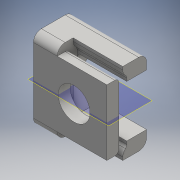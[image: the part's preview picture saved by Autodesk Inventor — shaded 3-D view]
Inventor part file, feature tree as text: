
AUTODESK INVENTOR PART (.ipt)
format: ipt  version: 2016 (Build 200138000, 138)  size: 255,488 bytes
history: native  units: mm
features: extrude x12, sketch x12, projected_geometry x5, fillet x3, plane x1, mirror x1
ambient origin geometry x8: Origin, YZ Plane, XZ Plane, XY Plane, X Axis, Y Axis, Z Axis, Center Point
bodies: Solid1 (feature_tree)
feature tree (34):
  extrude  "Extrusion1"  Depth=16.5mm
  sketch  "Sketch2"  dims[d2=11.0mm d3=0.0mm d4=6.0mm]
  extrude  "Extrusion2"  Depth=6.0mm
  extrude  "Extrusion3"  Depth=2.0mm
  extrude  "Extrusion4"  Depth=13.0mm
  extrude  "Extrusion5"  Depth=5.0mm
  extrude  "Extrusion6"  Depth=12.5mm TaperAngle=0.0deg
  extrude  "Extrusion7"  Depth=12.5mm TaperAngle=0.0deg
  extrude  "Extrusion8"  Depth=3.0mm TaperAngle=0.0deg
  extrude  "Extrusion9"  Depth=16.5mm
  extrude  "Extrusion10"  Depth=1.0mm
  plane  "Work Plane1"
  mirror  "Mirror1"
  extrude  "Extrusion11"  Depth=2.0mm TaperAngle=0.0deg
  fillet  "Fillet3"  Radius=2.0mm
  fillet  "Fillet4"  Radius=2.0mm
  fillet  "Fillet5"  Radius=2.0mm
  extrude  "Extrusion12"  Depth=3.0mm TaperAngle=0.0deg
  sketch  "Sketch1"  dims[d0=16.5mm d1=16.5mm]
  projected_geometry  "Projected Loop1"
  sketch  "Sketch3"  dims[d5=1.0mm d6=2.0mm]
  sketch  "Sketch4"  dims[d7=1.0mm d8=13.0mm]
  sketch  "Sketch5"  dims[d9=5.0mm d10=0.0mm d11=8.0mm]
  sketch  "Sketch6"  dims[d12=20.0mm d13=0.0mm d14=12.5mm d15=0.0mm]
  projected_geometry  "Projected Loop2"
  sketch  "Sketch7"  dims[d16=13.0mm d17=12.5mm d18=0.0mm]
  projected_geometry  "Projected Loop3"
  sketch  "Sketch8"  dims[d19=2.0mm d20=0.0mm d21=3.0mm d22=0.0mm]
  projected_geometry  "Projected Loop4"
  sketch  "Sketch10"  dims[d24=2.0mm d25=0.0mm d28=16.5mm]
  sketch  "Sketch11"  dims[d29=2.0mm d30=1.0mm]
  sketch  "Sketch12"  dims[d31=2.0mm d32=0.0mm d33=2.0mm d34=0.0mm d36=2.0mm d37=0.0mm d38=2.0mm d39=2.0mm]
  sketch  "Sketch13"  dims[d40=2.0mm d41=3.0mm d42=0.0mm]
  projected_geometry  "Projected Loop7"
